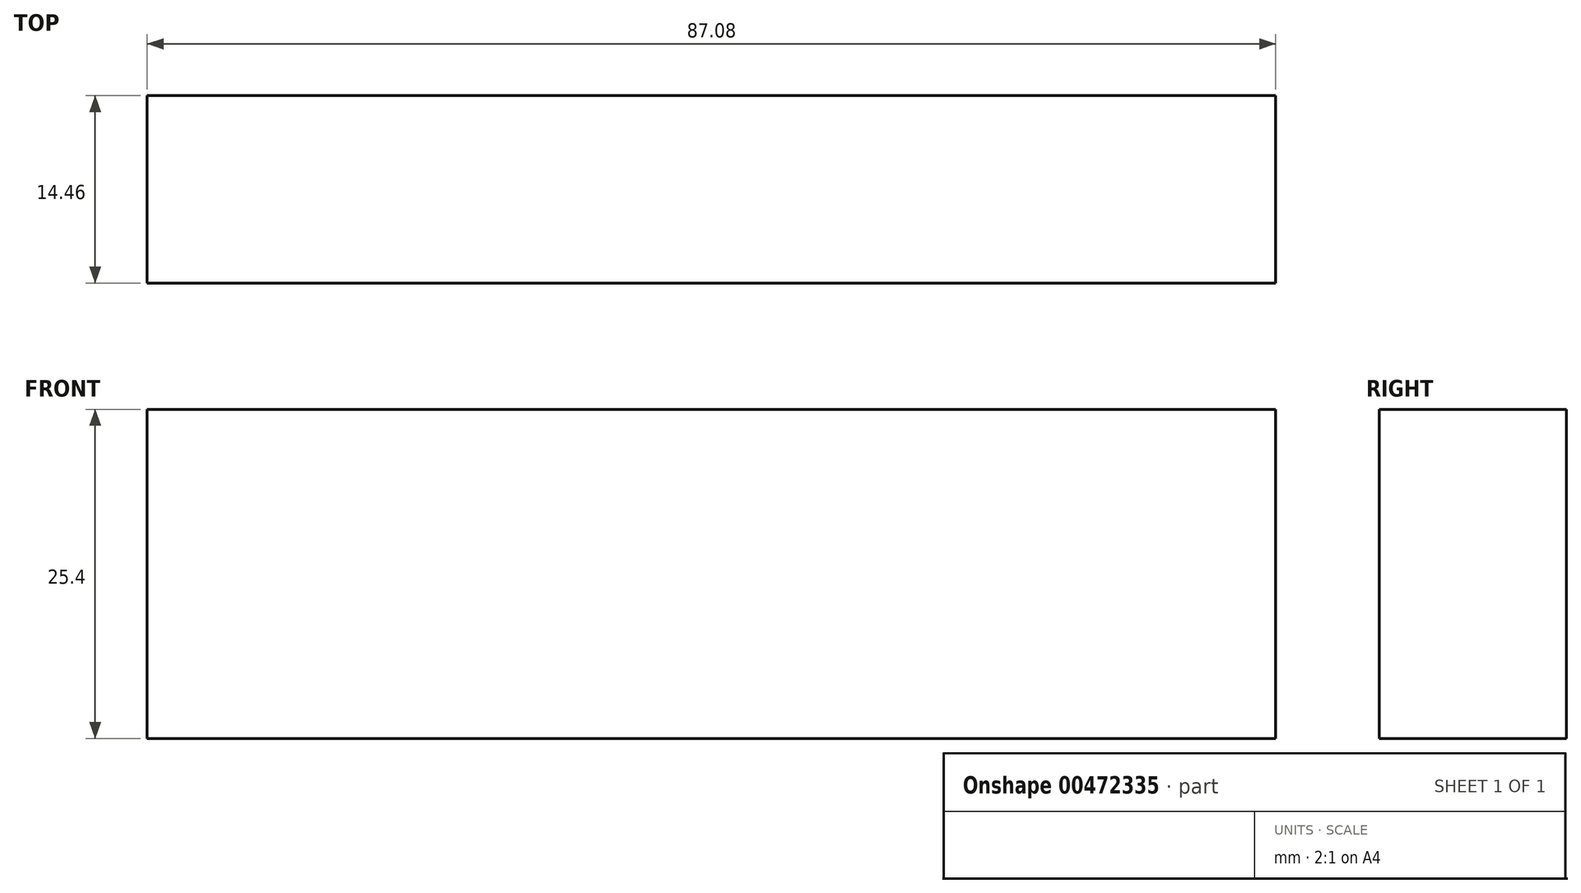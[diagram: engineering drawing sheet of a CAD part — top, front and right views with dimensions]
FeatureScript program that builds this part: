
annotation { "Feature Type Name" : "Feature", "Feature Type Description" : "" }
export const myFeature = defineFeature(function(context is Context, id is Id, definition is map)
    precondition{}
    {
        {
            var Q0;
            Q0=qCreatedBy(makeId("Top.planeOp"),FACE);
            var sketch = newSketch(context, id + "F0", { "sketchPlane" : qUnion([Q0])});
            skLineSegment(sketch, "E0.bottom", {"start": v(-77.25, 31.97) * mm, "end": v(-58.1, 31.97) * mm});
            skLineSegment(sketch, "E0.top", {"start": v(-77.25, 43.02) * mm, "end": v(-58.1, 43.02) * mm});
            skLineSegment(sketch, "E0.left", {"start": v(-77.25, 31.97) * mm, "end": v(-77.25, 43.02) * mm});
            skLineSegment(sketch, "E0.right", {"start": v(-58.1, 31.97) * mm, "end": v(-58.1, 43.02) * mm});
            skLineSegment(sketch, "E1.bottom", {"start": v(57, -31.9) * mm, "end": v(-30.08, -31.9) * mm});
            skLineSegment(sketch, "E1.top", {"start": v(57, -46.37) * mm, "end": v(-30.08, -46.37) * mm});
            skLineSegment(sketch, "E1.left", {"start": v(57, -31.9) * mm, "end": v(57, -46.37) * mm});
            skLineSegment(sketch, "E1.right", {"start": v(-30.08, -31.9) * mm, "end": v(-30.08, -46.37) * mm});
            skSolve(sketch);
        }
        {
            var Q0;
            Q0 = qSketchRegion(id + "FlcF7idsQ9DF1bA_0", true);
            var Q1;
            Q1=makeQuery(id+"F0.imprint","IMPRINT",FACE,{"disambiguationData":[TD([[makeQuery(id+"F0.imprint","IMPRINT",EDGE,{"derivedFrom":sQuery(id+"F0.wireOp",EDGE,"E1.bottom")}),1.0]])]});
            extrude(context, id + "F1", {"entities" : qUnion([Q0, Q1]), "depth" : 25.4 * mm});
        }
    });
